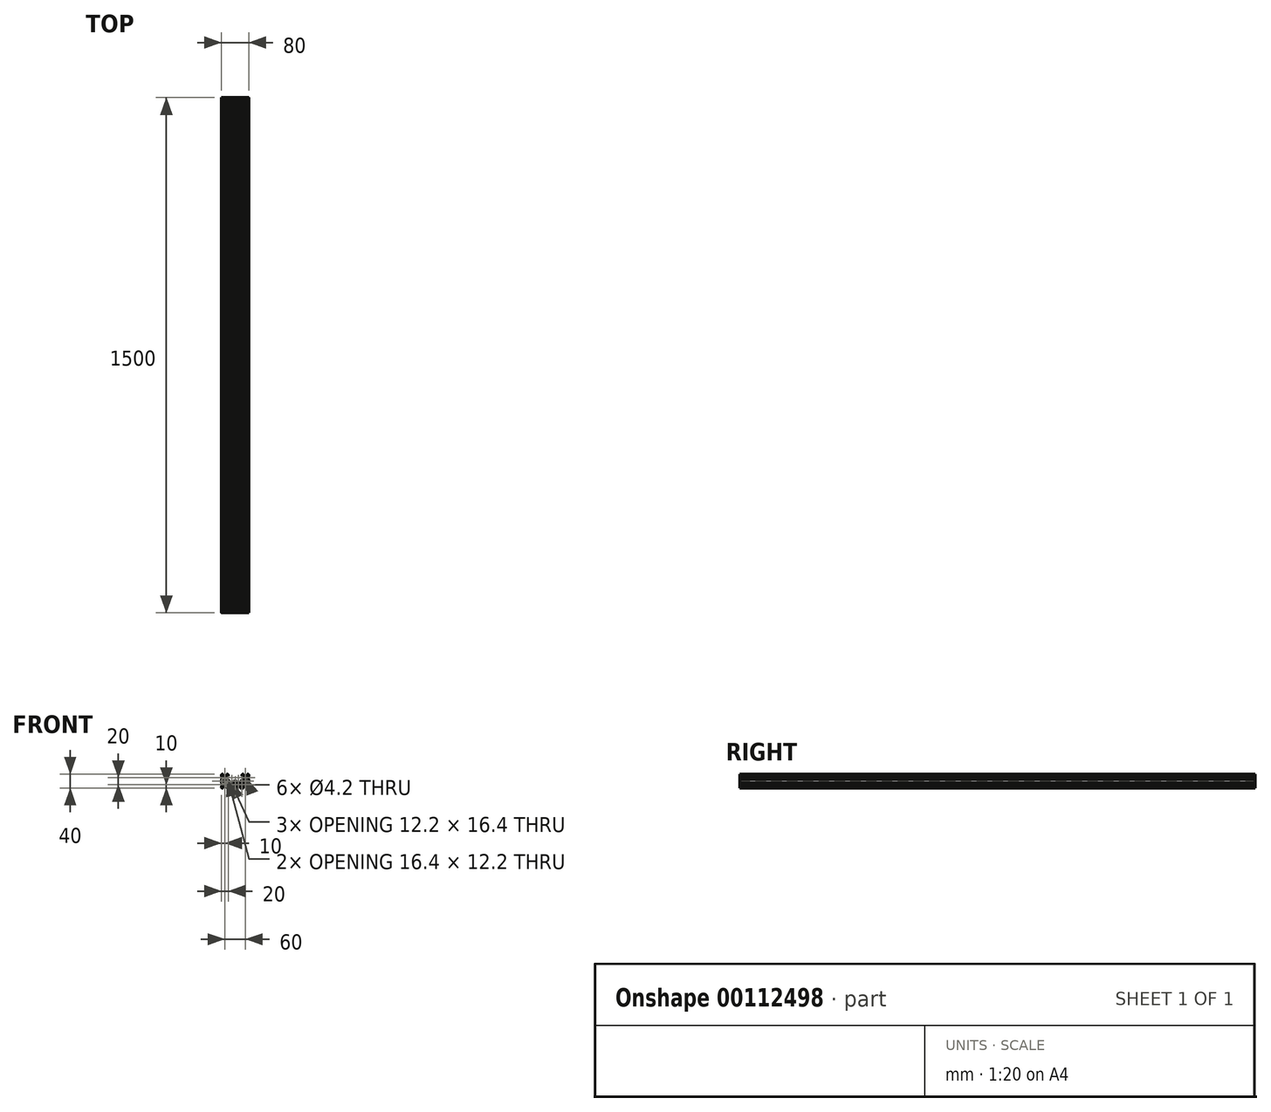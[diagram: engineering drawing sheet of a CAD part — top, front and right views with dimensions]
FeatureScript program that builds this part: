
annotation { "Feature Type Name" : "Feature", "Feature Type Description" : "" }
export const myFeature = defineFeature(function(context is Context, id is Id, definition is map)
    precondition{}
    {
        {
            var Q0;
            Q0=qCreatedBy(makeId("Front.planeOp"),FACE);
            var sketch = newSketch(context, id + "F0", { "sketchPlane" : qUnion([Q0])});
            skLineSegment(sketch, "E0", {"start": v(-38.2, 20) * mm, "end": v(-35.19, 20) * mm});
            skLineSegment(sketch, "E1", {"start": v(-20, 18.2) * mm, "end": v(-20, 15.19) * mm});
            skLineSegment(sketch, "E2", {"start": v(20, 0) * mm, "end": v(20, 4.81) * mm});
            skLineSegment(sketch, "E3", {"start": v(21.8, 20) * mm, "end": v(24.81, 20) * mm});
            skLineSegment(sketch, "E4", {"start": v(40, 18.2) * mm, "end": v(40, 15.19) * mm});
            skLineSegment(sketch, "E5", {"start": v(38.2, -20) * mm, "end": v(35.19, -20) * mm});
            skLineSegment(sketch, "E6", {"start": v(-40, -18.2) * mm, "end": v(-40, -15.19) * mm});
            skLineSegment(sketch, "E7", {"start": v(0, 21.7) * mm, "end": v(0, -26.3) * mm, "construction": true});
            skLineSegment(sketch, "E8.0", {"start": v(-38.2, -15.34) * mm, "end": v(-38.2, -13.39) * mm});
            skLineSegment(sketch, "E8.1", {"start": v(35.34, -18.2) * mm, "end": v(33.39, -18.2) * mm});
            skLineSegment(sketch, "E8.2", {"start": v(-35.34, 18.2) * mm, "end": v(-33.39, 18.2) * mm});
            skLineSegment(sketch, "E8.3", {"start": v(38.2, 15.34) * mm, "end": v(38.2, 13.39) * mm});
            skLineSegment(sketch, "E8.4", {"start": v(-21.8, 15.34) * mm, "end": v(-21.8, 13.39) * mm});
            skLineSegment(sketch, "E8.5", {"start": v(-20.74, -1.8) * mm, "end": v(-17.3, -1.8) * mm});
            skLineSegment(sketch, "E8.6", {"start": v(21.8, -0.74) * mm, "end": v(21.8, 2.7) * mm});
            skLineSegment(sketch, "E8.7", {"start": v(24.66, 18.2) * mm, "end": v(26.61, 18.2) * mm});
            skPoint(sketch, "E9.visualSharp", {"position": v(-40, 20) * mm});
            skArc(sketch, "E9.filletArc", {"start": v(-38.2, 20) * mm, "mid": v(-39.47, 19.47) * mm, "end": v(-40, 18.2) * mm});
            skPoint(sketch, "E10.visualSharp", {"position": v(-40, -20) * mm});
            skArc(sketch, "E10.filletArc", {"start": v(-40, -18.2) * mm, "mid": v(-39.47, -19.47) * mm, "end": v(-38.2, -20) * mm});
            skPoint(sketch, "E11.visualSharp", {"position": v(40, -20) * mm});
            skArc(sketch, "E11.filletArc", {"start": v(38.2, -20) * mm, "mid": v(39.47, -19.47) * mm, "end": v(40, -18.2) * mm});
            skPoint(sketch, "E12.visualSharp", {"position": v(40, 20) * mm});
            skArc(sketch, "E12.filletArc", {"start": v(40, 18.2) * mm, "mid": v(39.47, 19.47) * mm, "end": v(38.2, 20) * mm});
            skArc(sketch, "E13.filletArc", {"start": v(21.8, 20) * mm, "mid": v(20.53, 19.47) * mm, "end": v(20, 18.2) * mm});
            skPoint(sketch, "E14.visualSharp", {"position": v(-20, 20) * mm});
            skArc(sketch, "E14.filletArc", {"start": v(-20, 18.2) * mm, "mid": v(-20.53, 19.47) * mm, "end": v(-21.8, 20) * mm});
            skLineSegment(sketch, "E15", {"start": v(-38.2, 18.2) * mm, "end": v(-20, 0) * mm, "construction": true});
            skLineSegment(sketch, "E16", {"start": v(-21.8, 18.2) * mm, "end": v(-30, 10) * mm, "construction": true});
            skLineSegment(sketch, "E17", {"start": v(-24.81, 20) * mm, "end": v(-26.61, 18.2) * mm});
            skLineSegment(sketch, "E18", {"start": v(-35.19, 20) * mm, "end": v(-33.39, 18.2) * mm});
            skLineSegment(sketch, "E19.trimOffspring", {"start": v(-24.81, 20) * mm, "end": v(-21.8, 20) * mm});
            skLineSegment(sketch, "E20.trimOffspring", {"start": v(-26.61, 18.2) * mm, "end": v(-24.66, 18.2) * mm});
            skLineSegment(sketch, "E21", {"start": v(-40, 10) * mm, "end": v(-20, 10) * mm, "construction": true});
            skLineSegment(sketch, "E22.MirrorCS", {"start": v(-20, 4.81) * mm, "end": v(-21.8, 6.61) * mm});
            skLineSegment(sketch, "E23.MirrorCS", {"start": v(-20, 15.19) * mm, "end": v(-21.8, 13.39) * mm});
            skLineSegment(sketch, "E24.MirrorCS", {"start": v(-40, 4.81) * mm, "end": v(-38.2, 6.61) * mm});
            skLineSegment(sketch, "E25.MirrorCS", {"start": v(-40, 15.19) * mm, "end": v(-38.2, 13.39) * mm});
            skLineSegment(sketch, "E26.trimOffspring", {"start": v(-40, 15.19) * mm, "end": v(-40, 18.2) * mm});
            skLineSegment(sketch, "E27.trimOffspring", {"start": v(-38.2, 13.39) * mm, "end": v(-38.2, 15.34) * mm});
            skLineSegment(sketch, "E28.trimOffspring", {"start": v(-21.8, 6.61) * mm, "end": v(-21.8, 4.2) * mm});
            skLineSegment(sketch, "E29.trimOffspring", {"start": v(-20, 4.81) * mm, "end": v(-20, 0) * mm});
            skLineSegment(sketch, "E30.0", {"start": v(-36.4, 15.34) * mm, "end": v(-33.9, 12.84) * mm});
            skLineSegment(sketch, "E31.0", {"start": v(-35.34, 16.4) * mm, "end": v(-32.84, 13.9) * mm});
            skLineSegment(sketch, "E32.MirrorCS", {"start": v(-36.86, 4.2) * mm, "end": v(-33.9, 7.16) * mm});
            skLineSegment(sketch, "E33.MirrorCS", {"start": v(-36.24, 2.7) * mm, "end": v(-32.84, 6.1) * mm});
            skLineSegment(sketch, "E34", {"start": v(-33.9, 12.84) * mm, "end": v(-33.9, 7.16) * mm});
            skLineSegment(sketch, "E35.MirrorCS", {"start": v(-32.84, 13.9) * mm, "end": v(-27.16, 13.9) * mm});
            skLineSegment(sketch, "E36.MirrorCS", {"start": v(-26.1, 7.16) * mm, "end": v(-26.1, 12.84) * mm});
            skLineSegment(sketch, "E37.MirrorCS", {"start": v(-27.16, 6.1) * mm, "end": v(-32.84, 6.1) * mm});
            skLineSegment(sketch, "E38.trimOffspring", {"start": v(-27.16, 13.9) * mm, "end": v(-24.66, 16.4) * mm});
            skLineSegment(sketch, "E39.trimOffspring", {"start": v(-26.1, 12.84) * mm, "end": v(-23.6, 15.34) * mm});
            skLineSegment(sketch, "E40.trimOffspring", {"start": v(-26.1, 7.16) * mm, "end": v(-23.14, 4.2) * mm});
            skLineSegment(sketch, "E41.trimOffspring", {"start": v(-27.16, 6.1) * mm, "end": v(-23.76, 2.7) * mm});
            skLineSegment(sketch, "E42.trimOffspring", {"start": v(-38.2, 4.2) * mm, "end": v(-38.2, 6.61) * mm});
            skLineSegment(sketch, "E43.trimOffspring", {"start": v(-21.8, 2.7) * mm, "end": v(-21.8, -0.74) * mm});
            skLineSegment(sketch, "E44", {"start": v(-38.2, 15.34) * mm, "end": v(-36.4, 15.34) * mm});
            skPoint(sketch, "E45.orphan", {"position": v(-38.2, 17.14) * mm});
            skLineSegment(sketch, "E46.MirrorCS", {"start": v(-35.34, 18.2) * mm, "end": v(-35.34, 16.4) * mm});
            skPoint(sketch, "E47.orphan", {"position": v(-37.14, 18.2) * mm});
            skLineSegment(sketch, "E48", {"start": v(-30, 10) * mm, "end": v(-30, 20) * mm, "construction": true});
            skPoint(sketch, "E48.endSnap0", {"position": v(-30, 13.9) * mm});
            skLineSegment(sketch, "E49.MirrorCS", {"start": v(-24.66, 18.2) * mm, "end": v(-24.66, 16.4) * mm});
            skLineSegment(sketch, "E50.MirrorCS", {"start": v(-21.8, 15.34) * mm, "end": v(-23.6, 15.34) * mm});
            skCircle(sketch, "E51", {"center": v(-30, 10) * mm, "radius": 2.1 * mm});
            skLineSegment(sketch, "E52", {"start": v(-38.2, 2.7) * mm, "end": v(-36.24, 2.7) * mm});
            skLineSegment(sketch, "E53.0", {"start": v(-38.2, 4.2) * mm, "end": v(-36.86, 4.2) * mm});
            skLineSegment(sketch, "E54", {"start": v(-20, 0) * mm, "end": v(-40, 0) * mm, "construction": true});
            skLineSegment(sketch, "E55.MirrorCS", {"start": v(-27.16, -6.1) * mm, "end": v(-32.84, -6.1) * mm});
            skLineSegment(sketch, "E56.MirrorCS", {"start": v(-36.24, -2.7) * mm, "end": v(-32.84, -6.1) * mm});
            skLineSegment(sketch, "E57.MirrorCS", {"start": v(-38.2, -2.7) * mm, "end": v(-36.24, -2.7) * mm});
            skLineSegment(sketch, "E58.MirrorCS", {"start": v(-38.2, -4.2) * mm, "end": v(-36.86, -4.2) * mm});
            skLineSegment(sketch, "E59.MirrorCS", {"start": v(-40, -4.81) * mm, "end": v(-38.2, -6.61) * mm});
            skLineSegment(sketch, "E60.MirrorCS", {"start": v(-36.86, -4.2) * mm, "end": v(-33.9, -7.16) * mm});
            skLineSegment(sketch, "E61.MirrorCS", {"start": v(-33.9, -12.84) * mm, "end": v(-33.9, -7.16) * mm});
            skLineSegment(sketch, "E62.MirrorCS", {"start": v(-36.4, -15.34) * mm, "end": v(-33.9, -12.84) * mm});
            skLineSegment(sketch, "E63.MirrorCS", {"start": v(-38.2, -15.34) * mm, "end": v(-36.4, -15.34) * mm});
            skLineSegment(sketch, "E64.MirrorCS", {"start": v(-40, -15.19) * mm, "end": v(-38.2, -13.39) * mm});
            skLineSegment(sketch, "E65.MirrorCS", {"start": v(-35.34, -18.2) * mm, "end": v(-35.34, -16.4) * mm});
            skLineSegment(sketch, "E66.MirrorCS", {"start": v(-35.19, -20) * mm, "end": v(-33.39, -18.2) * mm});
            skLineSegment(sketch, "E67.MirrorCS", {"start": v(-35.34, -16.4) * mm, "end": v(-32.84, -13.9) * mm});
            skLineSegment(sketch, "E68.MirrorCS", {"start": v(-32.84, -13.9) * mm, "end": v(-27.16, -13.9) * mm});
            skLineSegment(sketch, "E69.MirrorCS", {"start": v(-27.16, -13.9) * mm, "end": v(-24.2, -16.86) * mm});
            skLineSegment(sketch, "E70.MirrorCS", {"start": v(-26.1, -12.84) * mm, "end": v(-22.7, -16.24) * mm});
            skLineSegment(sketch, "E71.MirrorCS", {"start": v(-26.1, -7.16) * mm, "end": v(-20.74, -1.8) * mm});
            skLineSegment(sketch, "E72.MirrorCS", {"start": v(-27.16, -6.1) * mm, "end": v(-21.8, -0.74) * mm});
            skLineSegment(sketch, "E73.MirrorCS", {"start": v(-26.1, -7.16) * mm, "end": v(-26.1, -12.84) * mm});
            skLineSegment(sketch, "E74.MirrorCS", {"start": v(-24.81, -20) * mm, "end": v(-26.61, -18.2) * mm});
            skCircle(sketch, "E75.MirrorC", {"center": v(-30, -10) * mm, "radius": 2.1 * mm});
            skLineSegment(sketch, "E76.MirrorCS", {"start": v(-21.8, 4.2) * mm, "end": v(-23.14, 4.2) * mm});
            skLineSegment(sketch, "E77.MirrorCS", {"start": v(-21.8, 2.7) * mm, "end": v(-23.76, 2.7) * mm});
            skLineSegment(sketch, "E78.trimOffspring", {"start": v(-40, -4.81) * mm, "end": v(-40, 4.81) * mm});
            skLineSegment(sketch, "E79.trimOffspring", {"start": v(-38.2, -6.61) * mm, "end": v(-38.2, -4.2) * mm});
            skLineSegment(sketch, "E80.trimOffspring", {"start": v(-38.2, -2.7) * mm, "end": v(-38.2, 2.7) * mm});
            skLineSegment(sketch, "E81.trimOffspring", {"start": v(-33.39, -18.2) * mm, "end": v(-35.34, -18.2) * mm});
            skLineSegment(sketch, "E82.trimOffspring", {"start": v(-35.19, -20) * mm, "end": v(-38.2, -20) * mm});
            skLineSegment(sketch, "E83.MirrorCS", {"start": v(-38.2, -18.2) * mm, "end": v(-20, 0) * mm, "construction": true});
            skLineSegment(sketch, "E84.MirrorCS", {"start": v(-24.2, -18.2) * mm, "end": v(-24.2, -16.86) * mm});
            skLineSegment(sketch, "E85.MirrorCS", {"start": v(-22.7, -18.2) * mm, "end": v(-22.7, -16.24) * mm});
            skLineSegment(sketch, "E86", {"start": v(-30, -10) * mm, "end": v(0, -10) * mm, "construction": true});
            skLineSegment(sketch, "E87.trimOffspring", {"start": v(-4.81, 0) * mm, "end": v(4.81, 0) * mm});
            skLineSegment(sketch, "E88.trimOffspring", {"start": v(-15.19, -20) * mm, "end": v(-24.81, -20) * mm});
            skLineSegment(sketch, "E89.trimOffspring", {"start": v(-6.61, -1.8) * mm, "end": v(-4.2, -1.8) * mm});
            skLineSegment(sketch, "E90.trimOffspring", {"start": v(-17.3, -18.2) * mm, "end": v(-22.7, -18.2) * mm});
            skLineSegment(sketch, "E91.trimOffspring", {"start": v(-24.2, -18.2) * mm, "end": v(-26.61, -18.2) * mm});
            skLineSegment(sketch, "E92", {"start": v(-20, 0) * mm, "end": v(-20, -18.2) * mm, "construction": true});
            skLineSegment(sketch, "E93.MirrorCS", {"start": v(-15.19, -20) * mm, "end": v(-13.39, -18.2) * mm});
            skLineSegment(sketch, "E94.MirrorCS", {"start": v(-15.8, -18.2) * mm, "end": v(-15.8, -16.86) * mm});
            skLineSegment(sketch, "E95.MirrorCS", {"start": v(-17.3, -18.2) * mm, "end": v(-17.3, -16.24) * mm});
            skLineSegment(sketch, "E96.MirrorCS", {"start": v(-12.84, -13.9) * mm, "end": v(-15.8, -16.86) * mm});
            skLineSegment(sketch, "E97.MirrorCS", {"start": v(-15.8, -18.2) * mm, "end": v(-13.39, -18.2) * mm});
            skLineSegment(sketch, "E98.MirrorCS", {"start": v(-13.9, -12.84) * mm, "end": v(-17.3, -16.24) * mm});
            skLineSegment(sketch, "E99.MirrorCS", {"start": v(-13.9, -7.16) * mm, "end": v(-13.9, -12.84) * mm});
            skLineSegment(sketch, "E100.MirrorCS", {"start": v(-4.81, -20) * mm, "end": v(-6.61, -18.2) * mm});
            skLineSegment(sketch, "E101.MirrorCS", {"start": v(-7.16, -13.9) * mm, "end": v(-12.84, -13.9) * mm});
            skLineSegment(sketch, "E102.MirrorCS", {"start": v(-13.9, -7.16) * mm, "end": v(-17.3, -3.76) * mm});
            skLineSegment(sketch, "E103.MirrorCS", {"start": v(-17.3, -1.8) * mm, "end": v(-17.3, -3.76) * mm});
            skLineSegment(sketch, "E104.MirrorCS", {"start": v(-15.8, -1.8) * mm, "end": v(-15.8, -3.14) * mm});
            skLineSegment(sketch, "E105.MirrorCS", {"start": v(-12.84, -6.1) * mm, "end": v(-15.8, -3.14) * mm});
            skLineSegment(sketch, "E106.MirrorCS", {"start": v(-7.16, -6.1) * mm, "end": v(-12.84, -6.1) * mm});
            skLineSegment(sketch, "E107.MirrorCS", {"start": v(-15.19, 0) * mm, "end": v(-13.39, -1.8) * mm});
            skLineSegment(sketch, "E108.MirrorCS", {"start": v(-15.8, -1.8) * mm, "end": v(-13.39, -1.8) * mm});
            skLineSegment(sketch, "E109.MirrorCS", {"start": v(-4.81, 0) * mm, "end": v(-6.61, -1.8) * mm});
            skCircle(sketch, "E110.MirrorC", {"center": v(-10, -10) * mm, "radius": 2.1 * mm});
            skLineSegment(sketch, "E111", {"start": v(-10, -10) * mm, "end": v(-10, 0) * mm, "construction": true});
            skLineSegment(sketch, "E112", {"start": v(-20, 0) * mm, "end": v(-15.19, 0) * mm});
            skLineSegment(sketch, "E113.MirrorCS", {"start": v(-4.2, -1.8) * mm, "end": v(-4.2, -3.14) * mm});
            skLineSegment(sketch, "E114.MirrorCS", {"start": v(-7.16, -6.1) * mm, "end": v(-4.2, -3.14) * mm});
            skLineSegment(sketch, "E115.MirrorCS", {"start": v(-2.7, -1.8) * mm, "end": v(-2.7, -3.76) * mm});
            skLineSegment(sketch, "E116.MirrorCS", {"start": v(-6.1, -7.16) * mm, "end": v(-2.7, -3.76) * mm});
            skLineSegment(sketch, "E117.MirrorCS", {"start": v(-6.1, -7.16) * mm, "end": v(-6.1, -12.84) * mm});
            skLineSegment(sketch, "E118.MirrorCS", {"start": v(-6.1, -12.84) * mm, "end": v(-2.7, -16.24) * mm});
            skLineSegment(sketch, "E119.MirrorCS", {"start": v(-7.16, -13.9) * mm, "end": v(-4.2, -16.86) * mm});
            skLineSegment(sketch, "E120.MirrorCS", {"start": v(-4.2, -18.2) * mm, "end": v(-4.2, -16.86) * mm});
            skLineSegment(sketch, "E121.MirrorCS", {"start": v(-2.7, -18.2) * mm, "end": v(-2.7, -16.24) * mm});
            skLineSegment(sketch, "E122.trimOffspring", {"start": v(-2.7, -1.8) * mm, "end": v(2.7, -1.8) * mm});
            skLineSegment(sketch, "E123.trimOffspring", {"start": v(-4.2, -18.2) * mm, "end": v(-6.61, -18.2) * mm});
            skLineSegment(sketch, "E124.MirrorCS", {"start": v(4.81, 0) * mm, "end": v(6.61, -1.8) * mm});
            skLineSegment(sketch, "E125.MirrorCS", {"start": v(4.2, -1.8) * mm, "end": v(4.2, -3.14) * mm});
            skLineSegment(sketch, "E126.MirrorCS", {"start": v(2.7, -1.8) * mm, "end": v(2.7, -3.76) * mm});
            skLineSegment(sketch, "E127.MirrorCS", {"start": v(6.1, -7.16) * mm, "end": v(2.7, -3.76) * mm});
            skLineSegment(sketch, "E128.MirrorCS", {"start": v(7.16, -6.1) * mm, "end": v(4.2, -3.14) * mm});
            skLineSegment(sketch, "E129.MirrorCS", {"start": v(6.1, -7.16) * mm, "end": v(6.1, -12.84) * mm});
            skLineSegment(sketch, "E130.MirrorCS", {"start": v(6.1, -12.84) * mm, "end": v(2.7, -16.24) * mm});
            skLineSegment(sketch, "E131.MirrorCS", {"start": v(2.7, -18.2) * mm, "end": v(2.7, -16.24) * mm});
            skLineSegment(sketch, "E132.MirrorCS", {"start": v(4.2, -18.2) * mm, "end": v(4.2, -16.86) * mm});
            skLineSegment(sketch, "E133.MirrorCS", {"start": v(4.2, -18.2) * mm, "end": v(6.61, -18.2) * mm});
            skLineSegment(sketch, "E134.MirrorCS", {"start": v(4.81, -20) * mm, "end": v(6.61, -18.2) * mm});
            skLineSegment(sketch, "E135.MirrorCS", {"start": v(7.16, -13.9) * mm, "end": v(12.84, -13.9) * mm});
            skCircle(sketch, "E136.MirrorC", {"center": v(10, -10) * mm, "radius": 2.1 * mm});
            skLineSegment(sketch, "E137.MirrorCS", {"start": v(7.16, -13.9) * mm, "end": v(4.2, -16.86) * mm});
            skLineSegment(sketch, "E138.MirrorCS", {"start": v(12.84, -13.9) * mm, "end": v(15.8, -16.86) * mm});
            skLineSegment(sketch, "E139.MirrorCS", {"start": v(15.8, -18.2) * mm, "end": v(15.8, -16.86) * mm});
            skLineSegment(sketch, "E140.MirrorCS", {"start": v(15.19, -20) * mm, "end": v(13.39, -18.2) * mm});
            skLineSegment(sketch, "E141.MirrorCS", {"start": v(17.3, -18.2) * mm, "end": v(17.3, -16.24) * mm});
            skLineSegment(sketch, "E142.MirrorCS", {"start": v(13.9, -12.84) * mm, "end": v(17.3, -16.24) * mm});
            skLineSegment(sketch, "E143.MirrorCS", {"start": v(13.9, -7.16) * mm, "end": v(13.9, -12.84) * mm});
            skLineSegment(sketch, "E144.MirrorCS", {"start": v(13.9, -7.16) * mm, "end": v(17.3, -3.76) * mm});
            skLineSegment(sketch, "E145.MirrorCS", {"start": v(17.3, -1.8) * mm, "end": v(17.3, -3.76) * mm});
            skLineSegment(sketch, "E146.MirrorCS", {"start": v(15.19, 0) * mm, "end": v(13.39, -1.8) * mm});
            skLineSegment(sketch, "E147.MirrorCS", {"start": v(15.8, -1.8) * mm, "end": v(15.8, -3.14) * mm});
            skLineSegment(sketch, "E148.MirrorCS", {"start": v(12.84, -6.1) * mm, "end": v(15.8, -3.14) * mm});
            skLineSegment(sketch, "E149.MirrorCS", {"start": v(7.16, -6.1) * mm, "end": v(12.84, -6.1) * mm});
            skLineSegment(sketch, "E150.trimOffspring", {"start": v(15.19, 0) * mm, "end": v(20, 0) * mm});
            skLineSegment(sketch, "E151.trimOffspring", {"start": v(13.39, -1.8) * mm, "end": v(15.8, -1.8) * mm});
            skLineSegment(sketch, "E152.trimOffspring", {"start": v(4.81, -20) * mm, "end": v(-4.81, -20) * mm});
            skLineSegment(sketch, "E153.trimOffspring", {"start": v(6.61, -18.2) * mm, "end": v(4.2, -18.2) * mm});
            skLineSegment(sketch, "E154.trimOffspring", {"start": v(17.3, -1.8) * mm, "end": v(20.74, -1.8) * mm});
            skLineSegment(sketch, "E155.trimOffspring", {"start": v(15.8, -18.2) * mm, "end": v(13.39, -18.2) * mm});
            skLineSegment(sketch, "E156.trimOffspring", {"start": v(2.7, -18.2) * mm, "end": v(-2.7, -18.2) * mm});
            skLineSegment(sketch, "E157.trimOffspring", {"start": v(4.2, -1.8) * mm, "end": v(6.61, -1.8) * mm});
            skLineSegment(sketch, "E158.MirrorCS", {"start": v(24.81, -20) * mm, "end": v(26.61, -18.2) * mm});
            skLineSegment(sketch, "E159.MirrorCS", {"start": v(24.2, -18.2) * mm, "end": v(26.61, -18.2) * mm});
            skLineSegment(sketch, "E160.MirrorCS", {"start": v(24.2, -18.2) * mm, "end": v(24.2, -16.86) * mm});
            skLineSegment(sketch, "E161.MirrorCS", {"start": v(22.7, -18.2) * mm, "end": v(22.7, -16.24) * mm});
            skLineSegment(sketch, "E162.MirrorCS", {"start": v(26.1, -12.84) * mm, "end": v(22.7, -16.24) * mm});
            skLineSegment(sketch, "E163.MirrorCS", {"start": v(27.16, -13.9) * mm, "end": v(24.2, -16.86) * mm});
            skLineSegment(sketch, "E164.MirrorCS", {"start": v(32.84, -13.9) * mm, "end": v(27.16, -13.9) * mm});
            skLineSegment(sketch, "E165.MirrorCS", {"start": v(26.1, -7.16) * mm, "end": v(26.1, -12.84) * mm});
            skLineSegment(sketch, "E166.MirrorCS", {"start": v(26.1, -7.16) * mm, "end": v(20.74, -1.8) * mm});
            skLineSegment(sketch, "E167.MirrorCS", {"start": v(27.16, -6.1) * mm, "end": v(21.8, -0.74) * mm});
            skLineSegment(sketch, "E168.MirrorCS", {"start": v(27.16, -6.1) * mm, "end": v(32.84, -6.1) * mm});
            skLineSegment(sketch, "E169.MirrorCS", {"start": v(36.24, -2.7) * mm, "end": v(32.84, -6.1) * mm});
            skLineSegment(sketch, "E170.MirrorCS", {"start": v(36.86, -4.2) * mm, "end": v(33.9, -7.16) * mm});
            skLineSegment(sketch, "E171.MirrorCS", {"start": v(38.2, -2.7) * mm, "end": v(36.24, -2.7) * mm});
            skLineSegment(sketch, "E172.MirrorCS", {"start": v(38.2, -4.2) * mm, "end": v(36.86, -4.2) * mm});
            skLineSegment(sketch, "E173.MirrorCS", {"start": v(40, -4.81) * mm, "end": v(38.2, -6.61) * mm});
            skLineSegment(sketch, "E174.MirrorCS", {"start": v(33.9, -12.84) * mm, "end": v(33.9, -7.16) * mm});
            skLineSegment(sketch, "E175.MirrorCS", {"start": v(36.4, -15.34) * mm, "end": v(33.9, -12.84) * mm});
            skLineSegment(sketch, "E176.MirrorCS", {"start": v(40, -15.19) * mm, "end": v(38.2, -13.39) * mm});
            skLineSegment(sketch, "E177.MirrorCS", {"start": v(38.2, -15.34) * mm, "end": v(36.4, -15.34) * mm});
            skLineSegment(sketch, "E178.MirrorCS", {"start": v(35.34, -18.2) * mm, "end": v(35.34, -16.4) * mm});
            skLineSegment(sketch, "E179.MirrorCS", {"start": v(35.34, -16.4) * mm, "end": v(32.84, -13.9) * mm});
            skLineSegment(sketch, "E180.MirrorCS", {"start": v(35.19, -20) * mm, "end": v(33.39, -18.2) * mm});
            skCircle(sketch, "E181.MirrorC", {"center": v(30, -10) * mm, "radius": 2.1 * mm});
            skLineSegment(sketch, "E182.trimOffspring", {"start": v(26.61, -18.2) * mm, "end": v(24.2, -18.2) * mm});
            skLineSegment(sketch, "E183.trimOffspring", {"start": v(24.81, -20) * mm, "end": v(15.19, -20) * mm});
            skLineSegment(sketch, "E184.trimOffspring", {"start": v(22.7, -18.2) * mm, "end": v(17.3, -18.2) * mm});
            skLineSegment(sketch, "E185.trimOffspring", {"start": v(40, -15.19) * mm, "end": v(40, -18.2) * mm});
            skLineSegment(sketch, "E186.trimOffspring", {"start": v(38.2, -13.39) * mm, "end": v(38.2, -15.34) * mm});
            skLineSegment(sketch, "E187.trimOffspring", {"start": v(38.2, -4.2) * mm, "end": v(38.2, -6.61) * mm});
            skLineSegment(sketch, "E188.MirrorCS", {"start": v(21.8, 2.7) * mm, "end": v(23.76, 2.7) * mm});
            skLineSegment(sketch, "E189.MirrorCS", {"start": v(21.8, 4.2) * mm, "end": v(23.14, 4.2) * mm});
            skLineSegment(sketch, "E190.MirrorCS", {"start": v(20, 4.81) * mm, "end": v(21.8, 6.61) * mm});
            skLineSegment(sketch, "E191.MirrorCS", {"start": v(26.1, 7.16) * mm, "end": v(23.14, 4.2) * mm});
            skLineSegment(sketch, "E192.MirrorCS", {"start": v(27.16, 6.1) * mm, "end": v(23.76, 2.7) * mm});
            skLineSegment(sketch, "E193.MirrorCS", {"start": v(27.16, 6.1) * mm, "end": v(32.84, 6.1) * mm});
            skLineSegment(sketch, "E194.MirrorCS", {"start": v(36.24, 2.7) * mm, "end": v(32.84, 6.1) * mm});
            skLineSegment(sketch, "E195.MirrorCS", {"start": v(36.86, 4.2) * mm, "end": v(33.9, 7.16) * mm});
            skLineSegment(sketch, "E196.MirrorCS", {"start": v(38.2, 4.2) * mm, "end": v(36.86, 4.2) * mm});
            skLineSegment(sketch, "E197.MirrorCS", {"start": v(38.2, 2.7) * mm, "end": v(36.24, 2.7) * mm});
            skLineSegment(sketch, "E198.MirrorCS", {"start": v(40, 4.81) * mm, "end": v(38.2, 6.61) * mm});
            skLineSegment(sketch, "E199.MirrorCS", {"start": v(40, 15.19) * mm, "end": v(38.2, 13.39) * mm});
            skLineSegment(sketch, "E200.MirrorCS", {"start": v(20, 15.19) * mm, "end": v(21.8, 13.39) * mm});
            skLineSegment(sketch, "E201.MirrorCS", {"start": v(26.1, 7.16) * mm, "end": v(26.1, 12.84) * mm});
            skLineSegment(sketch, "E202.MirrorCS", {"start": v(33.9, 12.84) * mm, "end": v(33.9, 7.16) * mm});
            skCircle(sketch, "E203.MirrorC", {"center": v(30, 10) * mm, "radius": 2.1 * mm});
            skLineSegment(sketch, "E204.MirrorCS", {"start": v(26.1, 12.84) * mm, "end": v(23.6, 15.34) * mm});
            skLineSegment(sketch, "E205.MirrorCS", {"start": v(21.8, 15.34) * mm, "end": v(23.6, 15.34) * mm});
            skLineSegment(sketch, "E206.MirrorCS", {"start": v(27.16, 13.9) * mm, "end": v(24.66, 16.4) * mm});
            skLineSegment(sketch, "E207.MirrorCS", {"start": v(32.84, 13.9) * mm, "end": v(27.16, 13.9) * mm});
            skLineSegment(sketch, "E208.MirrorCS", {"start": v(35.34, 16.4) * mm, "end": v(32.84, 13.9) * mm});
            skLineSegment(sketch, "E209.MirrorCS", {"start": v(35.34, 18.2) * mm, "end": v(35.34, 16.4) * mm});
            skLineSegment(sketch, "E210.MirrorCS", {"start": v(35.19, 20) * mm, "end": v(33.39, 18.2) * mm});
            skLineSegment(sketch, "E211.MirrorCS", {"start": v(24.81, 20) * mm, "end": v(26.61, 18.2) * mm});
            skLineSegment(sketch, "E212.MirrorCS", {"start": v(24.66, 18.2) * mm, "end": v(24.66, 16.4) * mm});
            skLineSegment(sketch, "E213.MirrorCS", {"start": v(38.2, 15.34) * mm, "end": v(36.4, 15.34) * mm});
            skLineSegment(sketch, "E214.MirrorCS", {"start": v(36.4, 15.34) * mm, "end": v(33.9, 12.84) * mm});
            skLineSegment(sketch, "E215.trimOffspring", {"start": v(35.19, 20) * mm, "end": v(38.2, 20) * mm});
            skLineSegment(sketch, "E216.trimOffspring", {"start": v(40, 4.81) * mm, "end": v(40, -4.81) * mm});
            skLineSegment(sketch, "E217.trimOffspring", {"start": v(20, 15.19) * mm, "end": v(20, 18.2) * mm});
            skLineSegment(sketch, "E218.trimOffspring", {"start": v(33.39, 18.2) * mm, "end": v(35.34, 18.2) * mm});
            skLineSegment(sketch, "E219.trimOffspring", {"start": v(38.2, 6.61) * mm, "end": v(38.2, 4.2) * mm});
            skLineSegment(sketch, "E220.trimOffspring", {"start": v(21.8, 13.39) * mm, "end": v(21.8, 15.34) * mm});
            skLineSegment(sketch, "E221.trimOffspring", {"start": v(21.8, 4.2) * mm, "end": v(21.8, 6.61) * mm});
            skLineSegment(sketch, "E222.trimOffspring", {"start": v(38.2, 2.7) * mm, "end": v(38.2, -2.7) * mm});
            skSolve(sketch);
        }
        {
            var Q0;
            Q0=makeQuery(id+"F0.imprint","IMPRINT",FACE,{"disambiguationData":[TD([[makeQuery(id+"F0.imprint","IMPRINT",EDGE,{"derivedFrom":sQuery(id+"F0.wireOp",EDGE,"E0")}),-1.0]])]});
            extrude(context, id + "F1", {"entities" : qUnion([Q0]), "depth" : 1500 * mm, "symmetric" : true});
        }
    });
